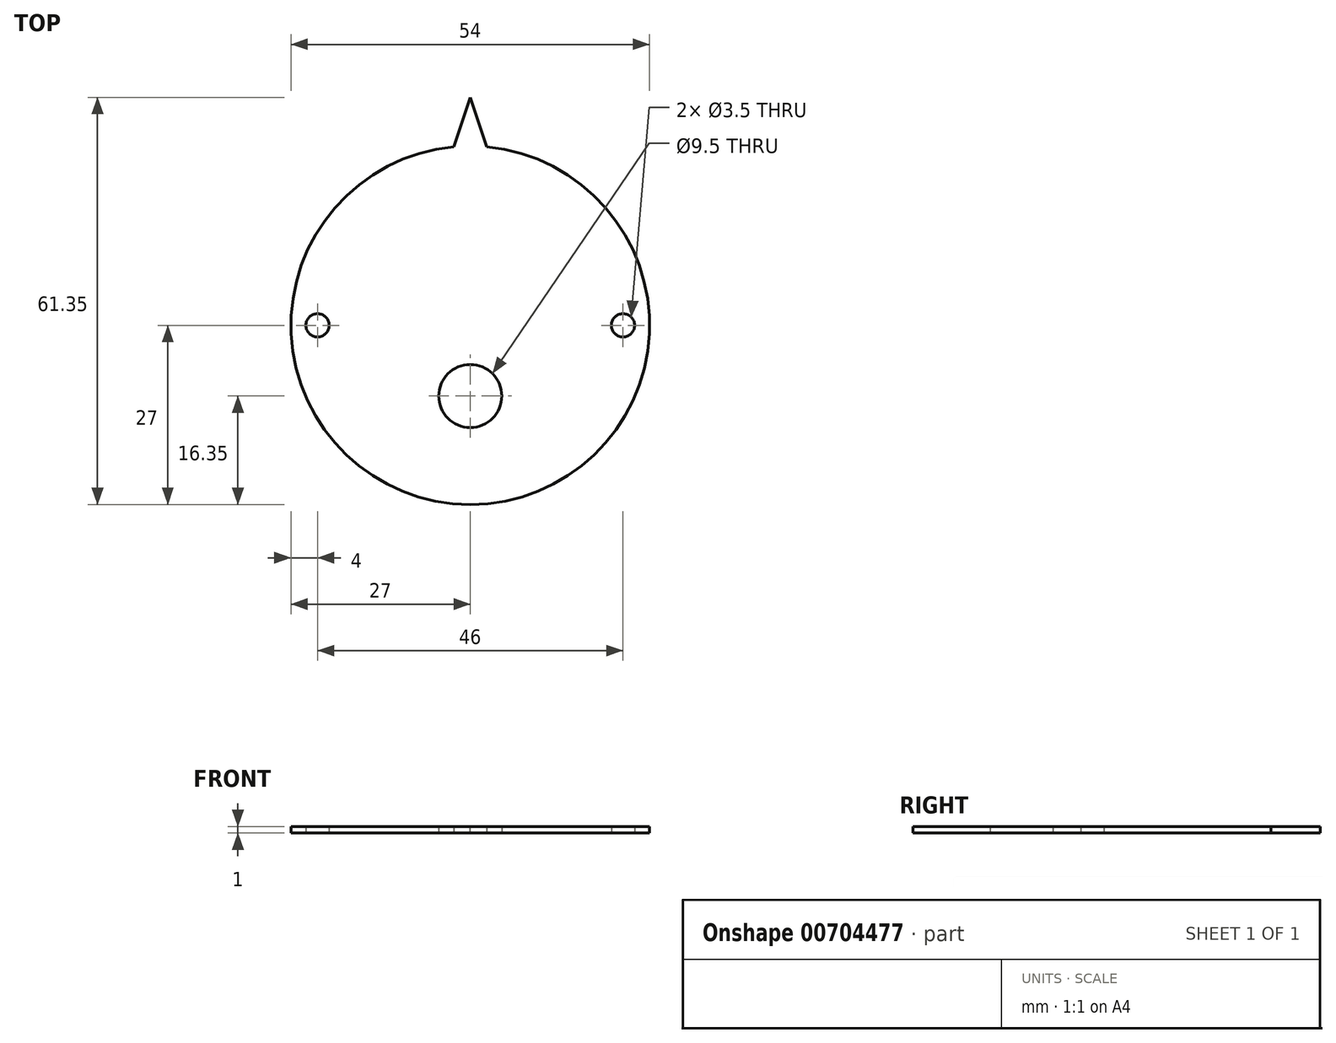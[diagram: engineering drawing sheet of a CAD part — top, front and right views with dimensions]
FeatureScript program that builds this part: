
annotation { "Feature Type Name" : "Feature", "Feature Type Description" : "" }
export const myFeature = defineFeature(function(context is Context, id is Id, definition is map)
    precondition{}
    {
        {
            var Q0;
            Q0=qCreatedBy(makeId("Top.planeOp"),FACE);
            var sketch = newSketch(context, id + "F0", { "sketchPlane" : qUnion([Q0])});
            skCircle(sketch, "E0", {"center": v(0, 0) * mm, "radius": 20.15 * mm, "construction": true});
            skArc(sketch, "E1", {"start": v(-2.5, 26.88) * mm, "mid": v(0, -27) * mm, "end": v(2.5, 26.88) * mm});
            skCircle(sketch, "E2", {"center": v(-23, 0) * mm, "radius": 1.75 * mm});
            skCircle(sketch, "E3", {"center": v(23, 0) * mm, "radius": 1.75 * mm});
            skLineSegment(sketch, "E4", {"start": v(-29.82, -10.65) * mm, "end": v(38.26, -10.65) * mm, "construction": true});
            skLineSegment(sketch, "E5.top", {"start": v(-2.5, 34.35) * mm, "end": v(2.5, 34.35) * mm});
            skLineSegment(sketch, "E6.trimOffspring", {"start": v(-2.5, 26.88) * mm, "end": v(-2.5, 34.35) * mm});
            skLineSegment(sketch, "E7.trimOffspring", {"start": v(2.5, 26.88) * mm, "end": v(2.5, 34.35) * mm});
            skCircle(sketch, "E8", {"center": v(0, -10.65) * mm, "radius": 4.75 * mm});
            skSolve(sketch);
        }
        {
            var Q0;
            Q0=makeQuery(id+"F0.imprint","IMPRINT",FACE,{"disambiguationData":[TD([[makeQuery(id+"F0.imprint","IMPRINT",EDGE,{"derivedFrom":sQuery(id+"F0.wireOp",EDGE,"E1")}),1.0]])]});
            extrude(context, id + "F1", {"entities" : qUnion([Q0]), "depth" : 1 * mm, "offsetDistance" : 25 * mm});
        }
        {
            var Q0;
            Q0=makeQuery(id+"F1.opExtrude","SWEPT_EDGE",EDGE,{"disambiguationData":[OSD([sQuery(id+"F0.wireOp",EDGE,"E5.top"),sQuery(id+"F0.wireOp",EDGE,"E6.trimOffspring")])]});
            var Q1;
            Q1=makeQuery(id+"F1.opExtrude","SWEPT_EDGE",EDGE,{"disambiguationData":[OSD([sQuery(id+"F0.wireOp",EDGE,"E5.top"),sQuery(id+"F0.wireOp",EDGE,"E7.trimOffspring")])]});
            chamfer(context, id + "F2", {"entities" : qUnion([Q0, Q1]), "chamferType" : ChamferType.TWO_OFFSETS, "width1" : 7.46 * mm, "oppositeDirection" : false, "width2" : 2.5 * mm, "tangentPropagation" : true});
        }
    });
